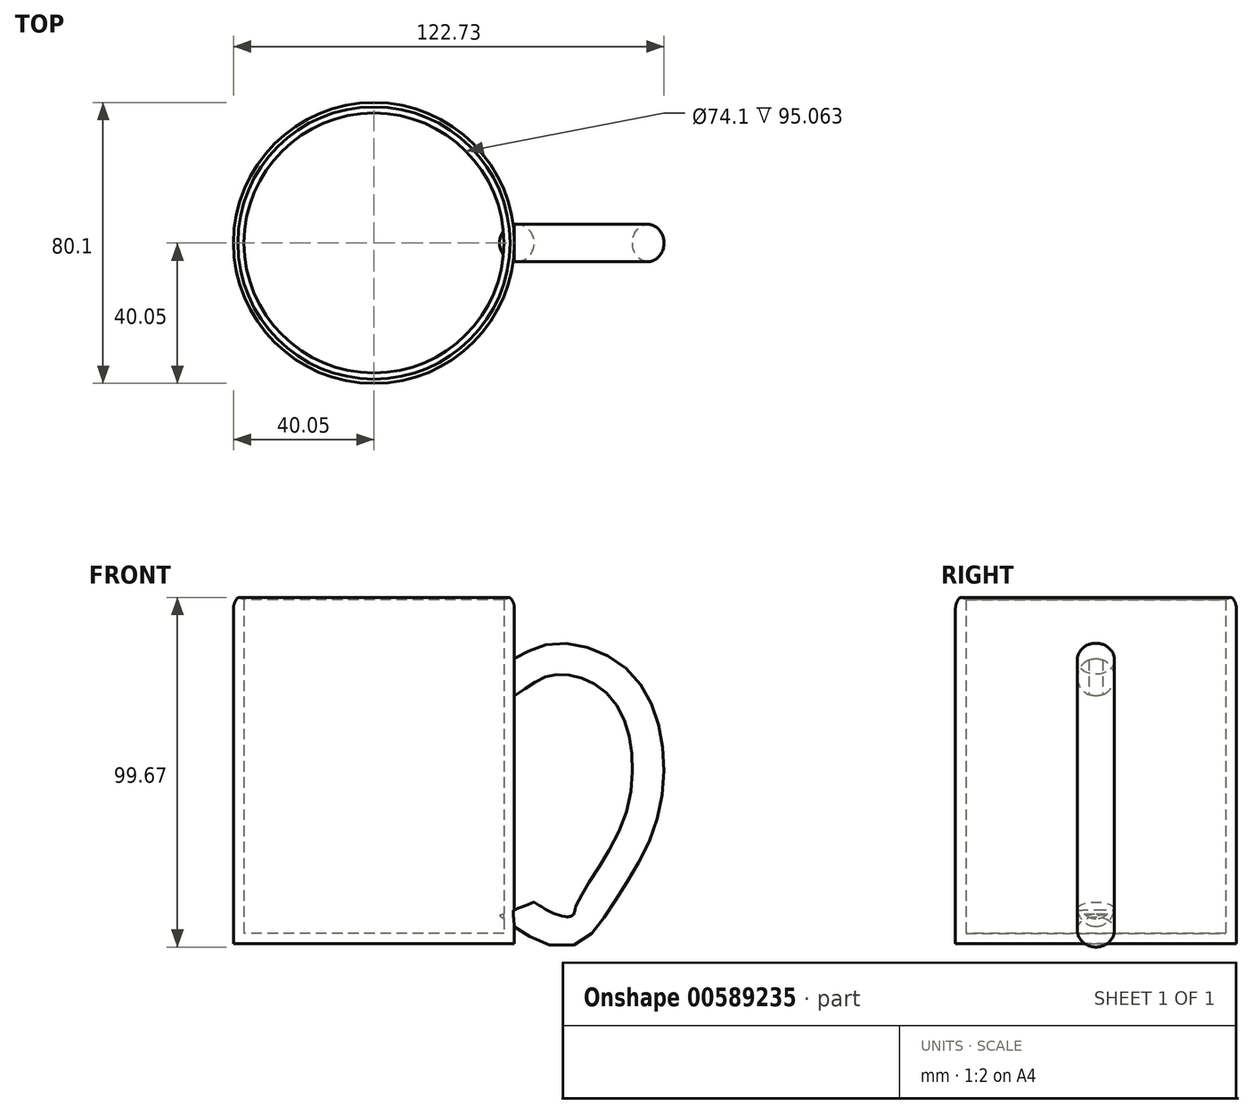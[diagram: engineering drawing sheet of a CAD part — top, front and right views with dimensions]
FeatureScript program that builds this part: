
annotation { "Feature Type Name" : "Feature", "Feature Type Description" : "" }
export const myFeature = defineFeature(function(context is Context, id is Id, definition is map)
    precondition{}
    {
        {
            var Q0;
            Q0=qCreatedBy(makeId("Top.planeOp"),FACE);
            var sketch = newSketch(context, id + "F0", { "sketchPlane" : qUnion([Q0])});
            skCircle(sketch, "E0", {"center": v(0, 0) * mm, "radius": 40.05 * mm});
            skSolve(sketch);
        }
        {
            var Q0;
            Q0 = qSketchRegion(id + "F0", true);
            extrude(context, id + "F1", {"entities" : qUnion([Q0]), "depth" : 100 * mm, "offsetDistance" : 25 * mm});
        }
        {
            var Q0;
            Q0=makeQuery(id+"F1.opExtrude","CAP_FACE",FACE,{"disambiguationData":[OSD([sQuery(id+"F0.wireOp",EDGE,"E0")])],"isStart":false});
            shell(context, id + "F2", {"entities" : qUnion([Q0]), "thickness" : 3 * mm});
        }
        {
            var Q0;
            Q0=makeQuery(id+"F1.opExtrude","CAP_EDGE",EDGE,{"disambiguationData":[OSD([sQuery(id+"F0.wireOp",EDGE,"E0")])],"isStart":false});
            fillet(context, id + "F3", {"entities" : qUnion([Q0]), "radius" : 5 * mm, "tangentPropagation" : true, "allowEdgeOverflow" : false});
        }
        {
            var Q0;
            {var subQ0=sQuery(id+"F0.wireOp",EDGE,"E0");Q0=makeQuery(id+"F3.opFillet","BLEND_EDGE",EDGE,{"blendedFrom":[makeQuery(id+"F1.opExtrude","CAP_EDGE",EDGE,{"disambiguationData":[OSD([subQ0])],"isStart":false}),makeQuery(id+"F2.opShell","OFFSET_FACE",FACE,{"disambiguationData":[OSD([subQ0]),TDD([makeQuery(id+"F1.opExtrude","SWEPT_FACE",FACE,{"disambiguationData":[OSD([subQ0])]})])]})],"blendedInto":[makeQuery(id+"F2.opShell","OFFSET_FACE",FACE,{"disambiguationData":[OSD([subQ0]),TDD([makeQuery(id+"F1.opExtrude","SWEPT_FACE",FACE,{"disambiguationData":[OSD([subQ0])]})])]})]});}
            chamfer(context, id + "F4", {"entities" : qUnion([Q0]), "width" : 1 * mm, "tangentPropagation" : true});
        }
        {
            var Q0;
            Q0=qCreatedBy(makeId("Right.planeOp"),FACE);
            cPlane(context, id + "F5", {"entities" : qUnion([Q0]), "cplaneType" : CPlaneType.OFFSET, "offset" : 40 * mm, "width" : 150 * mm, "height" : 150 * mm});
        }
        {
            var Q0;
            Q0=qCreatedBy(id+"F5.planeOp",FACE);
            var sketch = newSketch(context, id + "F6", { "sketchPlane" : qUnion([Q0])});
            skCircle(sketch, "E1", {"center": v(0, 75.94) * mm, "radius": 5.3 * mm});
            skSolve(sketch);
        }
        {
            var Q0;
            Q0=qCreatedBy(makeId("Front.planeOp"),FACE);
            var sketch = newSketch(context, id + "F7", { "sketchPlane" : qUnion([Q0])});
            skFitSpline(sketch, "E2", {"points": [v(40.5, 76) * mm, v(51.96, 80.75) * mm, v(67.77, 75.61) * mm, v(76.87, 59.8) * mm, v(75.68, 35.29) * mm, v(64.22, 13.94) * mm, v(54.33, 4.06) * mm, v(43.26, 8.4) * mm, v(40.5, 10.38) * mm], "startDerivative": vector(92.8, 57.24) * mm, "endDerivative": vector(-35.3, 26.56) * mm});
            skSolve(sketch);
        }
        {
            var Q0;
            Q0 = qSketchRegion(id + "F6", true);
            var Q1;
            Q1 = qConstructionFilter(qBodyType(qCreatedBy(id + "F7" ,EDGE), BodyType.WIRE), ConstructionObject.NO);
            sweep(context, id + "F8", {"operationType" : NewBodyOperationType.ADD, "profiles" : qUnion([Q0]), "path" : qUnion([Q1])});
        }
    });
